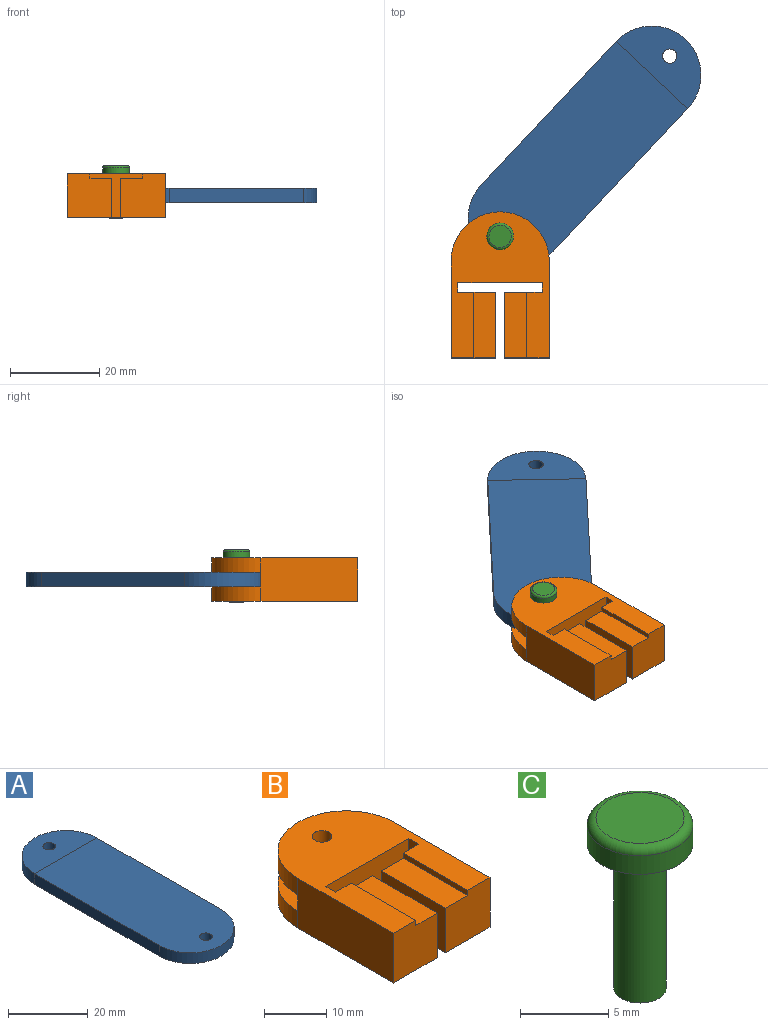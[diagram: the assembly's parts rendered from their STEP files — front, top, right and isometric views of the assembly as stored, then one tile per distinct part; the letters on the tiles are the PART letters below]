
ASSEMBLY  parts=3 mates=2
PART A: 9 faces, bbox 22x66x3.3 mm
  f0: plane 44x3.26mm, normal (-1,0,0), area 143.4mm2, adj f1,f4,f5,f6
  f1: cylinder r=11mm len=22mm, axis (0,0,-1), area 112.7mm2, adj f0,f2,f4,f5
  f2: plane 44x3.26mm, normal (1,0,0), area 143.4mm2, adj f1,f4,f5,f6
  f3: cylinder r=1.6mm len=3.26mm, axis (0,0,-1), area 32.8mm2, adj f4,f5
  f4: plane 55.02x22.02mm, normal (0,0,1), area 1150mm2, adj f0,f1,f2,f3,f7
  f5: plane 66x22mm, normal (0,0,-1), area 1332mm2, adj f0,f1,f2,f3,f6,f8
  f6: cylinder r=11mm len=22mm, axis (0,0,-1), area 112.5mm2, adj f0,f2,f5,f7
  f7: plane 22.02x11.02mm, normal (0,0,1), area 182mm2, adj f4,f6,f8
  f8: cylinder r=1.6mm len=3.25mm, axis (0,0,1), area 32.7mm2, adj f5,f7
PART B: 29 faces, bbox 22x32.7x9.8 mm
  f0: plane 14.7x8.78mm, normal (-1,0,0), area 129.1mm2, adj f3,f5,f20,f27
  f1: plane 14.7x8.78mm, normal (1,0,0), area 129.1mm2, adj f3,f11,f18,f28
  f2: plane 32.72x22mm, normal (0,0,1), area 444.7mm2, adj f5,f6,f7,f8,f10,f11,f12,f13
  f3: plane 32.72x22mm, normal (0,0,-1), area 575mm2, adj f0,f1,f5,f8,f9,f10,f11,f12
  f4: plane 22x11mm, normal (0,0,1), area 166.7mm2, adj f9,f16,f21,f22,f23,f24,f25,f26
  f5: plane 10.1x9.78mm, normal (0,-1,0), area 93.7mm2, adj f0,f2,f3,f8,f19,f20
  f6: cylinder r=11mm len=22mm, axis (0,0,-1), area 112.3mm2, adj f2,f8,f10,f15
  f7: cylinder r=1.6mm len=3.25mm, axis (0,0,-1), area 32.7mm2, adj f2,f15
  f8: plane 21.72x9.78mm, normal (1,0,0), area 212.4mm2, adj f2,f3,f5,f6,f9,f16
  f9: cylinder r=11mm len=22mm, axis (0,0,-1), area 112.3mm2, adj f3,f4,f8,f10
  f10: plane 21.72x9.78mm, normal (-1,0,0), area 212.4mm2, adj f2,f3,f6,f9,f11,f16
  f11: plane 10x9.78mm, normal (0,-1,0), area 92.9mm2, adj f1,f2,f3,f10,f17,f18
  f12: plane 9.78x2.2mm, normal (1,0,0), area 21.5mm2, adj f2,f3,f13,f28
  f13: plane 18.9x9.78mm, normal (0,-1,0), area 184.8mm2, adj f2,f3,f12,f14
  f14: plane 9.78x2.2mm, normal (-1,0,0), area 21.5mm2, adj f2,f3,f13,f27
  f15: plane 22x11mm, normal (0,0,-1), area 182mm2, adj f6,f7,f16
  f16: plane 22x3.28mm, normal (0,1,0), area 72.2mm2, adj f4,f8,f10,f15
  f17: plane 14.7x1mm, normal (1,0,0), area 14.7mm2, adj f2,f11,f18,f28
  f18: plane 14.7x4.86mm, normal (0,0,1), area 71.4mm2, adj f1,f11,f17,f28
  f19: plane 14.7x1mm, normal (-1,0,0), area 14.7mm2, adj f2,f5,f20,f27
  f20: plane 14.7x5.05mm, normal (0,0,1), area 74.2mm2, adj f0,f5,f19,f27
  f21: plane 3.25x3mm, normal (-1,0,0), area 9.7mm2, adj f3,f4,f22,f26
  f22: plane 3.25x2.6mm, normal (-0.5,0.87,0), area 9.8mm2, adj f3,f4,f21,f23
  f23: plane 3.25x2.6mm, normal (0.5,0.87,0), area 9.7mm2, adj f3,f4,f22,f24
  f24: plane 3.25x3mm, normal (1,0,0), area 9.7mm2, adj f3,f4,f23,f25
  f25: plane 3.25x2.6mm, normal (0.5,-0.87,0), area 9.7mm2, adj f3,f4,f24,f26
  f26: plane 3.25x2.6mm, normal (-0.5,-0.87,0), area 9.8mm2, adj f3,f4,f21,f25
  f27: plane 9.78x8.55mm, normal (0,1,0), area 78.6mm2, adj f0,f2,f3,f14,f19,f20
  f28: plane 9.78x8.45mm, normal (0,1,0), area 77.8mm2, adj f1,f2,f3,f12,f17,f18
PART C: 6 faces, bbox 6.5x6.5x11.8 mm
  f0: cylinder r=3mm len=6mm, axis (0,0,-1), area 24.5mm2, adj f2,f5
  f1: plane 5x5mm, normal (0,0,1), area 19.6mm2, adj f5
  f2: plane 6x6mm, normal (0,0,-1), area 21.2mm2, adj f0,f3
  f3: cylinder r=1.5mm len=10mm, axis (0,0,1), area 94.2mm2, adj f2,f4
  f4: plane 3x3mm, normal (0,0,-1), area 7.1mm2, adj f3
  f5: torus R=2.5mm, axis (0,0,1), area 13.9mm2, adj f0,f1
PLACE A rot(axis=(0,0,-1),43.3deg) t=(-251.35,-245.27,83.87)mm
PLACE B t=(-50.26,-273.68,83.87)mm fixed
PLACE C rot(axis=(0,0,-1),43.3deg) t=(-73.05,-23.03,93.68)mm
MATE revolute A.f3 <-> B.f7  axis (0,0,-1) through (-72.67,-22.63,88.75)mm
MATE fastened C.f0 <-> A.f3  axis (0,0,-1) through (-72.67,-22.63,83.68)mm
